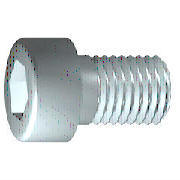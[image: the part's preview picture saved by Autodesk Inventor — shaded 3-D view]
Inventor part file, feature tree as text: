
AUTODESK INVENTOR PART (.ipt)
format: ipt  version: 2017 (Build 210142000, 142)  size: 184,832 bytes
history: native  units: mm (DEFAULTED — no unit token found)
features: sketch x2, extrude x1, plane x1, fillet x1
ambient origin geometry x7: Origin, YZ Plane, XY Plane, X Axis, Y Axis, Z Axis, Center Point
bodies: Solid1 (feature_tree), Body (feature_tree)
feature tree (5):
  extrude  "Slot"  Depth=4.0mm
  plane  "Work Plane1"
  fillet  "Fillet2"  Radius=4.0mm
  sketch  "Sketch1"  dims[d1=20.0mm d2=0.429515mm d3=4.0mm]
  sketch  "Sketch2"  dims[d4=2.0mm d5=60.0deg d6=4.0mm d7=4.0mm d8=3.464102mm d9=7.0mm d10=90.0deg d11=10.0mm d12=0.0mm d13=20.0mm d14=0.0mm d15=0.429415mm d16=0.429415mm d17=0.4mm d19=0.0mm d26=30.0mm d27=45.0deg d28=0.0mm d29=0.0mm d30=0.1mm]
